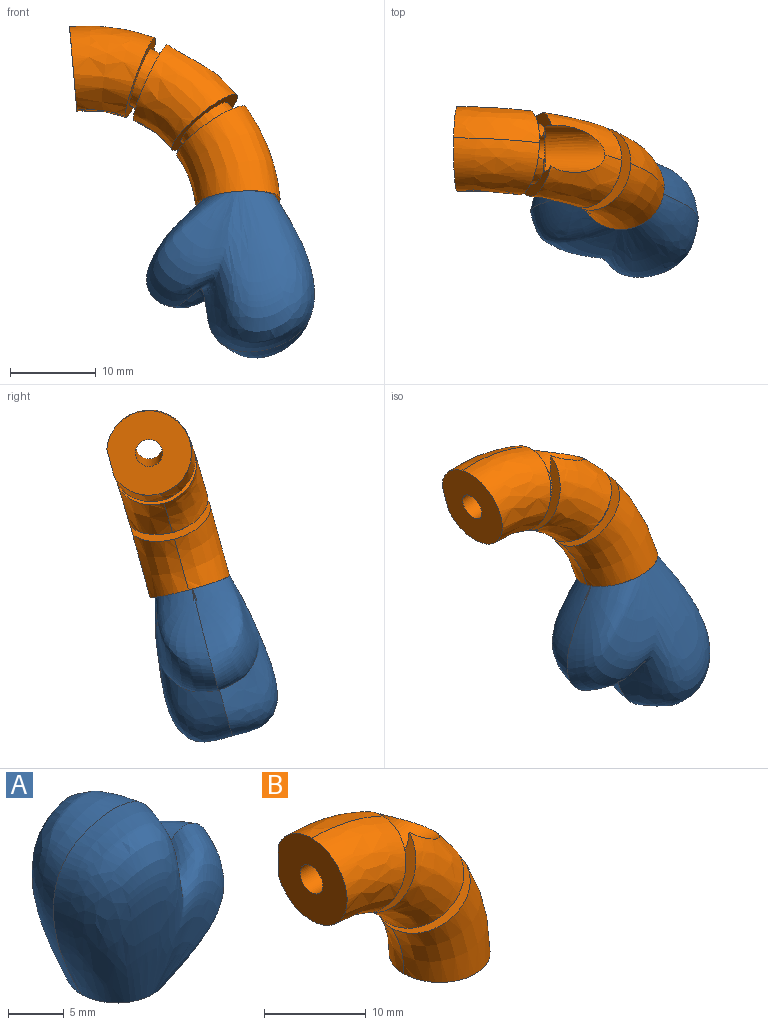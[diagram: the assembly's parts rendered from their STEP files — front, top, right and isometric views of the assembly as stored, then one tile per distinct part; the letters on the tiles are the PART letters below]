
ASSEMBLY  parts=2 mates=1
PART A: 3 faces, bbox 23.5x20.6x22.4 mm
  f0: plane 12.96x12.96mm, normal (0,0,-1), area 63.6mm2, adj f1,f2
  f1: bspline ~19.52x18.47mm, area 451.4mm2, adj f0,f2
  f2: bspline ~19.52x18.47mm, area 451.4mm2, adj f0,f1
PART B: 25 faces, bbox 23x10.6x23 mm
  f0: bspline ~6.94x4.57mm, area 13.1mm2, adj f1,f2,f5,f6,f24
  f1: bspline ~6.94x4.57mm, area 13.1mm2, adj f0,f2,f5,f6,f24
  f2: cylinder r=1.59mm len=10.16mm, axis (-1,0,0), area 98.8mm2, adj f0,f1,f5,f14,f24
  f3: bspline ~9.44x9.13mm, area 38.1mm2, adj f5,f14,f18,f20
  f4: bspline ~9.89x5.21mm, area 58.9mm2, adj f5,f14,f18,f20
  f5: plane 9.88x9.16mm, normal (0.9,0,-0.43), area 36.6mm2, adj f0,f1,f2,f3,f4,f18,f20
  f6: plane 9.65x8.06mm, normal (-0.86,0,0.5), area 28.7mm2, adj f0,f1,f7,f8,f17,f22,f23,f24
  f7: bspline ~6.89x6.74mm, area 38.1mm2, adj f6,f9,f17,f22
  f8: bspline ~9.05x8.75mm, area 41.3mm2, adj f6,f9,f17,f22,f23
  f9: plane 9.68x8.24mm, normal (0.56,0,-0.83), area 36.8mm2, adj f7,f8,f16,f17,f19,f22
  f10: plane 9.64x8.65mm, normal (-0.49,0,0.87), area 36.8mm2, adj f11,f12,f15,f16,f19,f21
  f11: bspline ~7.96x4.95mm, area 43.8mm2, adj f10,f13,f15,f21
  f12: bspline ~11.24x8.32mm, area 67.7mm2, adj f10,f13,f15,f21
  f13: plane 9.93x9.67mm, normal (0,0,-1), area 76.6mm2, adj f11,f12,f15,f21
  f14: plane 9.93x9.63mm, normal (-1,0,0), area 68.7mm2, adj f2,f3,f4,f18,f20
  f15: bspline ~11.6x11.25mm, area 143.3mm2, adj f10,f11,f12,f13
  f16: bspline ~6.78x4.94mm, area 15.7mm2, adj f9,f10,f19
  f17: bspline ~12.48x12.4mm, area 107.1mm2, adj f6,f7,f8,f9,f23
  f18: bspline ~11.19x9.89mm, area 124.6mm2, adj f3,f4,f5,f14
  f19: bspline ~6.78x4.94mm, area 15.7mm2, adj f9,f10,f16
  f20: plane 8.48x5mm, normal (0,1,0), area 27.1mm2, adj f3,f4,f5,f14
  f21: plane 9.64x5.5mm, normal (0,1,0), area 31.1mm2, adj f10,f11,f12,f13
  f22: plane 8.06x7.84mm, normal (0,1,0), area 27.1mm2, adj f6,f7,f8,f9
  f23: cylinder r=2.76mm len=6.93mm, axis (1,0,0), area 43.4mm2, adj f6,f8,f17,f24
  f24: plane 5.54x3.48mm, normal (1,0,0), area 8.3mm2, adj f0,f1,f2,f6,f23
PLACE A rot(axis=(0.01,0.99,-0.13),175deg) t=(-42.24,-3.39,-35.48)mm
PLACE B rot(axis=(-0.95,-0.31,-0.04),15.8deg) t=(-61.49,1.67,-20)mm
MATE fastened A.f0 <-> B.f13  axis (0.08,-0.26,-0.96) through (-42.35,-7.73,-34.32)mm
